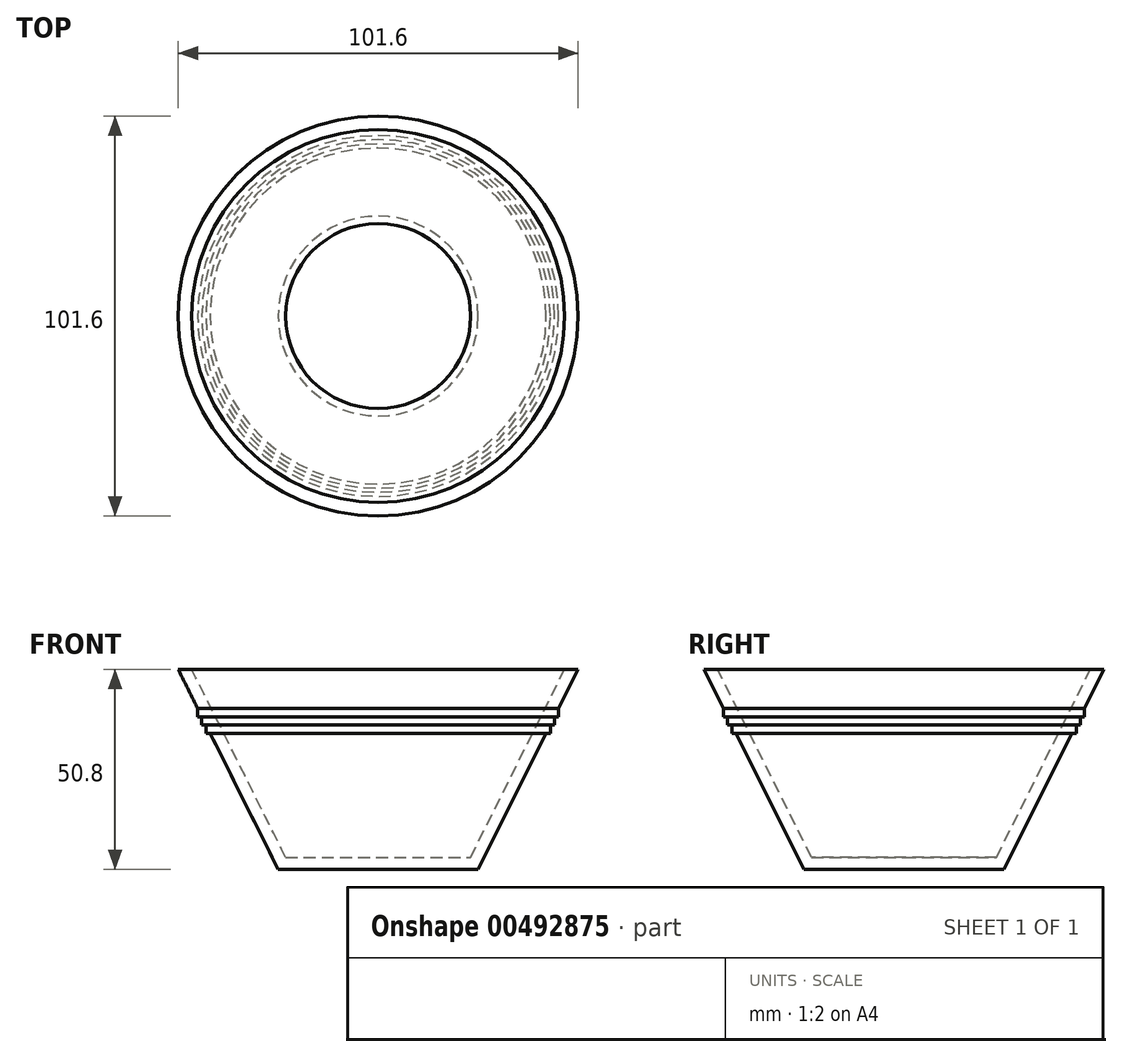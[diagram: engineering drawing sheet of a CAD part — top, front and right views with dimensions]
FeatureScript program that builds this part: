
annotation { "Feature Type Name" : "Feature", "Feature Type Description" : "" }
export const myFeature = defineFeature(function(context is Context, id is Id, definition is map)
    precondition{}
    {
        {
            var Q0;
            Q0=qCreatedBy(makeId("Front.planeOp"),FACE);
            var sketch = newSketch(context, id + "F0", { "sketchPlane" : qUnion([Q0])});
            skLineSegment(sketch, "E0", {"start": v(0, 0) * mm, "end": v(0, 50.8) * mm, "construction": true});
            skLineSegment(sketch, "E1", {"start": v(0, 0) * mm, "end": v(25.4, 0) * mm});
            skLineSegment(sketch, "E2", {"start": v(25.4, 0) * mm, "end": v(50.8, 50.8) * mm});
            skLineSegment(sketch, "E3.0", {"start": v(23.5, 3.07) * mm, "end": v(47.36, 50.8) * mm});
            skLineSegment(sketch, "E3.1", {"start": v(0, 3.07) * mm, "end": v(23.5, 3.07) * mm});
            skLineSegment(sketch, "E4", {"start": v(0, 3.07) * mm, "end": v(0, 0) * mm});
            skLineSegment(sketch, "E5", {"start": v(47.36, 50.8) * mm, "end": v(50.8, 50.8) * mm});
            skLineSegment(sketch, "E6", {"start": v(45.85, 40.9) * mm, "end": v(45.85, 38.8) * mm});
            skLineSegment(sketch, "E7", {"start": v(44.8, 38.8) * mm, "end": v(45.85, 38.8) * mm});
            skLineSegment(sketch, "E8", {"start": v(44.8, 38.8) * mm, "end": v(44.8, 36.69) * mm});
            skLineSegment(sketch, "E9", {"start": v(44.8, 36.69) * mm, "end": v(43.74, 36.69) * mm});
            skLineSegment(sketch, "E10", {"start": v(43.74, 36.69) * mm, "end": v(43.74, 34.58) * mm});
            skLineSegment(sketch, "E11", {"start": v(43.74, 34.58) * mm, "end": v(42.7, 34.58) * mm});
            skSolve(sketch);
        }
        {
            var Q0;
            Q0 = qSketchRegion(id + "F0", true);
            var Q1;
            Q1=sQuery(id+"F0.wireOp",EDGE,"E0");
            revolve(context, id + "F1", {"entities" : qUnion([Q0]), "axis" : qUnion([Q1]), "revolveType" : RevolveType.FULL});
        }
    });
